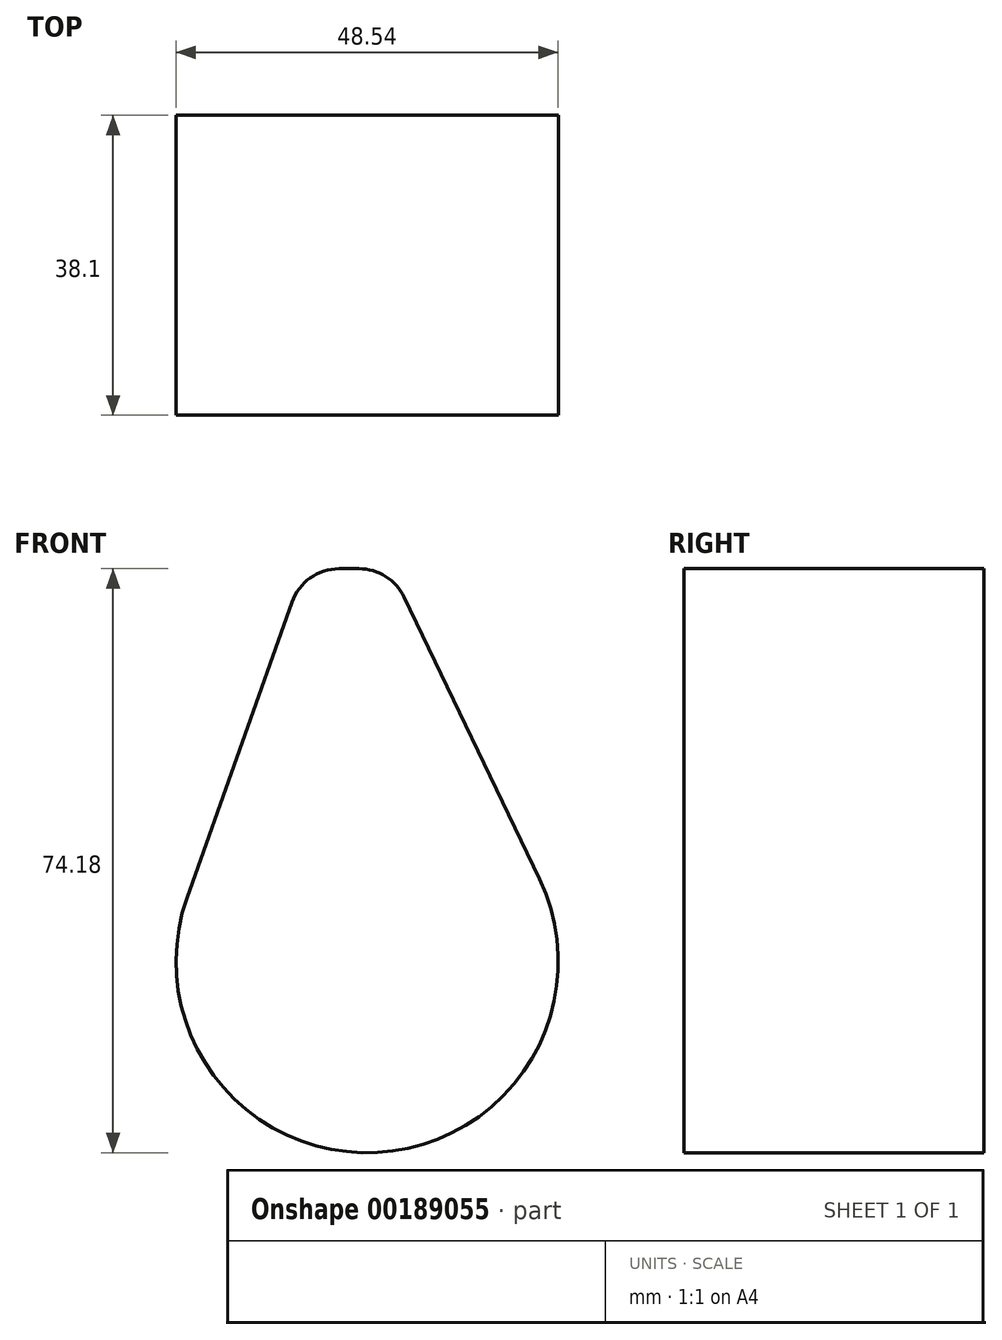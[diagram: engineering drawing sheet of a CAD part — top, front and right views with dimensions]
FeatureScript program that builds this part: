
annotation { "Feature Type Name" : "Feature", "Feature Type Description" : "" }
export const myFeature = defineFeature(function(context is Context, id is Id, definition is map)
    precondition{}
    {
        {
            var Q0;
            Q0=qCreatedBy(makeId("Front.planeOp"),FACE);
            var sketch = newSketch(context, id + "F0", { "sketchPlane" : qUnion([Q0])});
            skArc(sketch, "E0", {"start": v(-22.88, 8.12) * mm, "mid": v(1.3, -24.24) * mm, "end": v(21.89, 10.5) * mm});
            skLineSegment(sketch, "E1", {"start": v(-22.88, 8.12) * mm, "end": v(-9.55, 45.69) * mm});
            skLineSegment(sketch, "E2", {"start": v(-3.56, 49.91) * mm, "end": v(-1.02, 49.91) * mm});
            skLineSegment(sketch, "E3", {"start": v(4.7, 46.31) * mm, "end": v(21.89, 10.5) * mm});
            skPoint(sketch, "E4.visualSharp", {"position": v(2.98, 49.91) * mm});
            skArc(sketch, "E4.filletArc", {"start": v(4.7, 46.31) * mm, "mid": v(2.36, 48.94) * mm, "end": v(-1.02, 49.91) * mm});
            skPoint(sketch, "E5.visualSharp", {"position": v(-8.05, 49.91) * mm});
            skArc(sketch, "E5.filletArc", {"start": v(-3.56, 49.91) * mm, "mid": v(-7.22, 48.75) * mm, "end": v(-9.55, 45.69) * mm});
            skSolve(sketch);
        }
        {
            var Q0;
            Q0 = qSketchRegion(id + "F0", true);
            extrude(context, id + "F1", {"entities" : qUnion([Q0]), "depth" : 38.1 * mm});
        }
    });
